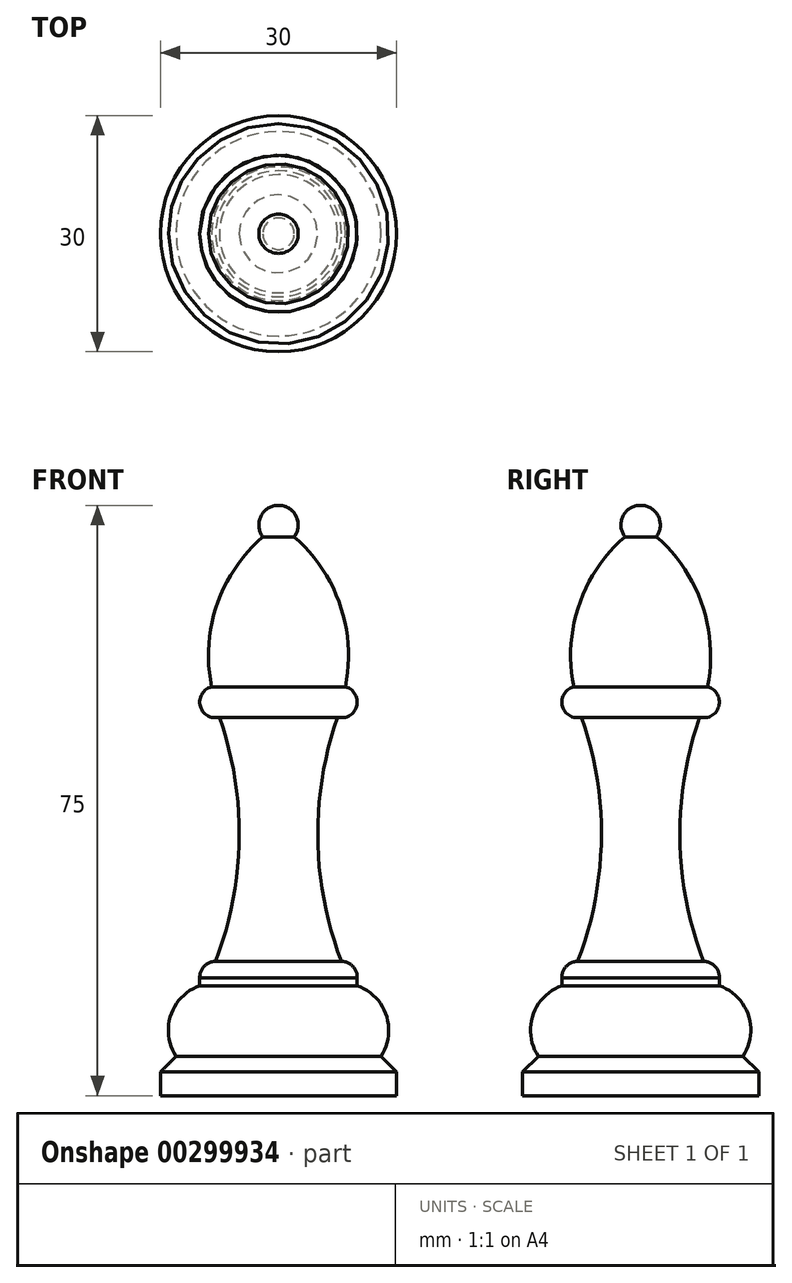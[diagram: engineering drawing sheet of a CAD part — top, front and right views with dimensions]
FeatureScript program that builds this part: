
annotation { "Feature Type Name" : "Feature", "Feature Type Description" : "" }
export const myFeature = defineFeature(function(context is Context, id is Id, definition is map)
    precondition{}
    {
        {
            var Q0;
            Q0=qCreatedBy(makeId("Front.planeOp"),FACE);
            var sketch = newSketch(context, id + "F0", { "sketchPlane" : qUnion([Q0])});
            skArc(sketch, "E0", {"start": v(2, -4) * mm, "mid": v(2.24, -1.38) * mm, "end": v(0, 0) * mm});
            skArc(sketch, "E1", {"start": v(8.5, -23.06) * mm, "mid": v(7.82, -12.65) * mm, "end": v(2, -4) * mm});
            skArc(sketch, "E2", {"start": v(8.5, -26.93) * mm, "mid": v(10, -25) * mm, "end": v(8.5, -23.06) * mm});
            skLineSegment(sketch, "E3", {"start": v(8.5, -26.93) * mm, "end": v(7.5, -26.93) * mm});
            skArc(sketch, "E4", {"start": v(7.5, -26.93) * mm, "mid": v(5, -42.49) * mm, "end": v(8, -57.95) * mm});
            skArc(sketch, "E5", {"start": v(10, -60.03) * mm, "mid": v(9.44, -58.57) * mm, "end": v(8, -57.95) * mm});
            skLineSegment(sketch, "E6", {"start": v(10, -60.03) * mm, "end": v(10, -61.03) * mm});
            skArc(sketch, "E7", {"start": v(13, -70) * mm, "mid": v(13.69, -64.78) * mm, "end": v(10, -61.03) * mm});
            skLineSegment(sketch, "E8", {"start": v(13, -70) * mm, "end": v(15, -72) * mm});
            skLineSegment(sketch, "E9", {"start": v(15, -72) * mm, "end": v(15, -75) * mm});
            skLineSegment(sketch, "E10", {"start": v(15, -75) * mm, "end": v(0, -75) * mm});
            skLineSegment(sketch, "E11", {"start": v(0, -75) * mm, "end": v(0, 0) * mm});
            skSolve(sketch);
        }
        {
            var Q0;
            Q0=makeQuery(id+"F0.imprint","IMPRINT",FACE,{"disambiguationData":[TD([[makeQuery(id+"F0.imprint","IMPRINT",EDGE,{"derivedFrom":sQuery(id+"F0.wireOp",EDGE,"E0")}),1.0]])]});
            var Q1;
            Q1=sQuery(id+"F0.wireOp",EDGE,"E11");
            revolve(context, id + "F1", {"entities" : qUnion([Q0]), "axis" : qUnion([Q1]), "revolveType" : RevolveType.FULL});
        }
    });
